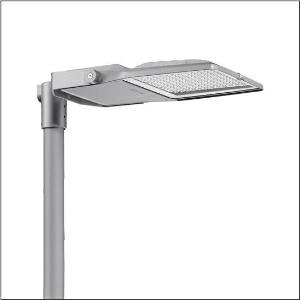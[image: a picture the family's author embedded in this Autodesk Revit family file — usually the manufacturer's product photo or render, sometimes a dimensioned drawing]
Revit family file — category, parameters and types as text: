
# Revit family: floodlight_fl_21_iq_midi___pl61_5xa7781f2c3a_20a4
name_source: partatom
category: Lighting Fixtures
units: mm (PartAtom-declared; Revit-internal decimal feet)

## family parameters
Cut with Voids When Loaded = No
Host = Face
Light Source = No
Part Type = Normal
Room Calculation Point = No
Round Connector Dimension = Use Diameter
Shared = No

## types (1)
- --- (1 x LED, 35100 lm, 270.2 W, 3000K)
    Apparent Load = 270 VA
    CIE Flux Codes = 33 65 98 100 100
    Color Rendering = 70
    Color Temperature = 3000K
    Default Elevation = 1800 mm
    Description = Floodlight FL 21 iQ midi, floodlight, primary light control with lens, of PMMA, primary optical cover: protective disc, of toughened safety glass, transparent, light distribution: PL61, light emission: direct distribution, installation type: surface-mounted, LED, High Power LED, rated luminous flux: 35.100lm, luminous efficacy: 130lm/W, light colour: 730, colour temperature: 3000K, control gear: ECG iQ, control: optimised constant luminous flux control (CLO 2.0), Desk-Remote (wireless, voltage-free reading and setting of iQ features in the workshop via application-optimized NFC function/RFID function), Light-Fading, Smart-Wire, Night-Set, Lumen-Switch, Temp-Guard, Auto-Match, with terminal, 6-pole, mains connection: 220..240V, AC, 50/60Hz, start of lifetime: 270W, end of service life: 287W, reduction: 117W, luminaire housing, of diecast aluminium, powder-coated, Siteco® metallic grey (DB 702S), corrosivity category C5 mid according to DIN EN ISO 12944, sealing non-destructively replaceable, please order mast flange separately, mast bracket, of steel, galvanised, powder-coated, Siteco® metallic grey (DB 702S), protection rating (complete): IP66, insulation class (complete): insulation class II (safety insulation), certification: CE, ENEC, VDE, protection symbol: D, impact resistance: IK08, permissible operating ambient temperature: -40..+40°C, permissible operating ambient temperature for outdoor applications: -40..+50°C, standard: DIN EN 12944, LABS conformity tested according to VDMA 24364:2018-05, packaging unit: 1 piece

Light Distribution: PL61
    Height = 76 mm
    Lamp = 1 x LED
    Lamp Light Flux = 35100 lm
    Lamp Power = 270.2 W
    Lamp count = 1
    Length = 657 mm
    Luminous efficacy = 130 lm/W
    Manufacturer = Siteco
    ModVariant = No
    Model = 5XA7781F2C3A
    Number of Poles = 1
    OnlyDefault = Yes
    Power Factor = 1
    Product Name = Floodlight FL 21 iQ midi | PL61
    Product group = floodlight | pylon annexe
    ProductGroupID = 6200
    Protection Class = Protection class II
    Protection Degree = IP 66
    RLX_Detail_Level = 1
    RLX_Emergency_Light_Flux = 0 lm
    RLX_Emergency_Type = 0
    RLX_Emergency_Type_DB = No
    RlxData = <blob elided: 153785 chars, md5=aee00d77>
    Socket = socket
    Standby Power = 0 W
    System Light Flux = 35100 lm
    System Power = 270 W
    Type Comments = factory setting: luminous flux: 100 % | dim-lin: 254 | 620 mA
    Type Image = l_1007123.jpg
    URL = http://relux.com
    VarID = @adj_077335
    Voltage = 0 V
    Weight = 0.00 kg
    Width = 442 mm

## geometry (parser evidence)
native form markers: Blend x4, Sweep x14
no freeform markers — native parametric forms only
